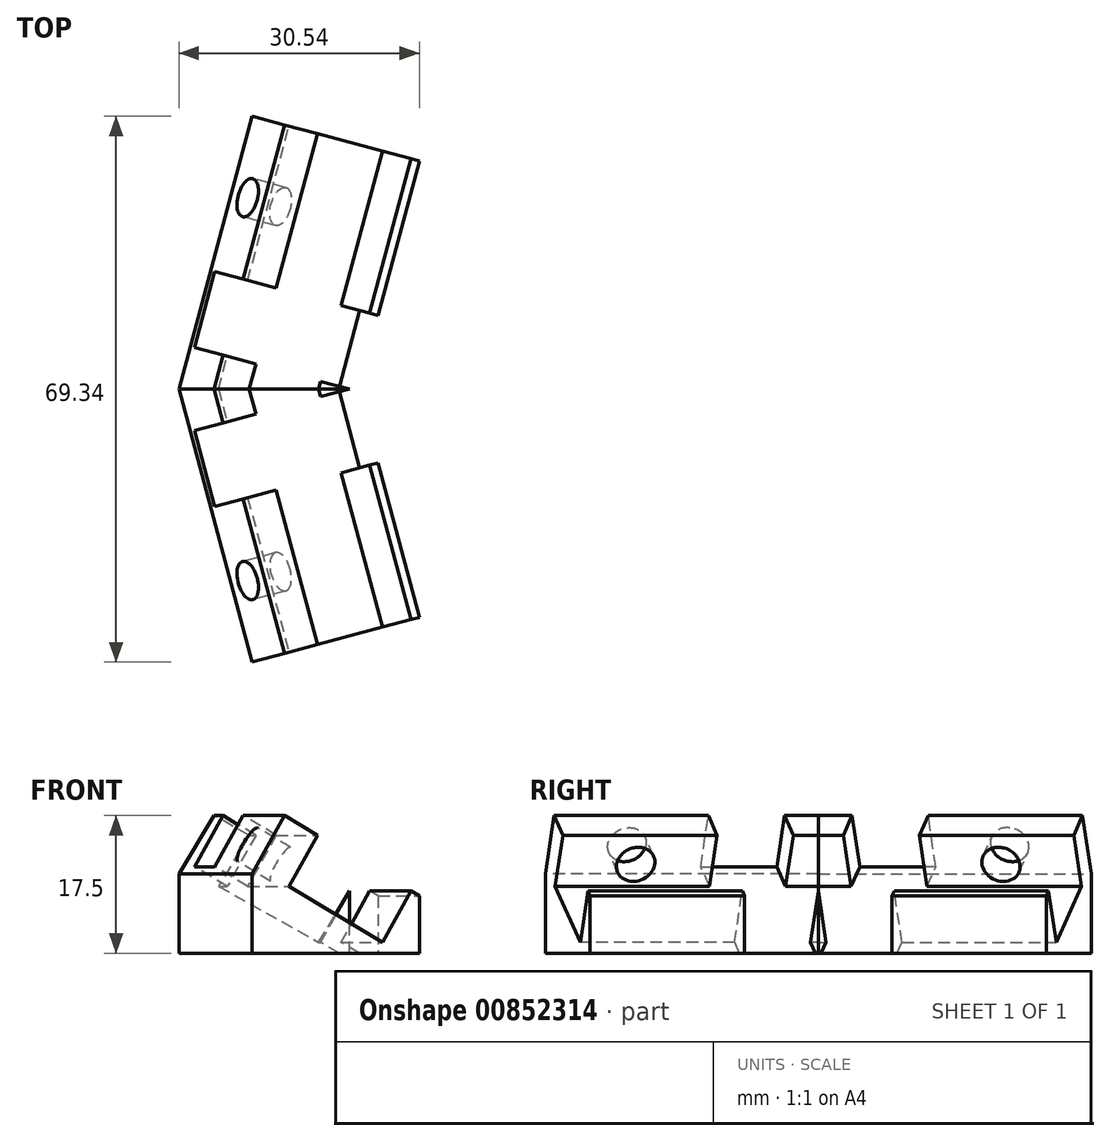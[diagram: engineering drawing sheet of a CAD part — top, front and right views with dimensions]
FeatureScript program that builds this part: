
annotation { "Feature Type Name" : "Feature", "Feature Type Description" : "" }
export const myFeature = defineFeature(function(context is Context, id is Id, definition is map)
    precondition{}
    {
        {
            var Q0;
            Q0=qCreatedBy(makeId("Top.planeOp"),FACE);
            var sketch = newSketch(context, id + "F0", { "sketchPlane" : qUnion([Q0])});
            skLineSegment(sketch, "E0", {"start": v(0, 0) * mm, "end": v(7.76, 28.98) * mm});
            skLineSegment(sketch, "E1", {"start": v(7.76, 28.98) * mm, "end": v(-13.49, 34.67) * mm});
            skLineSegment(sketch, "E2", {"start": v(-13.49, 34.67) * mm, "end": v(-22.78, 0) * mm});
            skLineSegment(sketch, "E3", {"start": v(-22.78, 0) * mm, "end": v(-13.49, -34.67) * mm});
            skLineSegment(sketch, "E4", {"start": v(-13.49, -34.67) * mm, "end": v(7.76, -28.98) * mm});
            skLineSegment(sketch, "E5", {"start": v(7.76, -28.98) * mm, "end": v(0, 0) * mm});
            skSolve(sketch);
        }
        {
            var Q0;
            Q0=makeQuery(id+"F0.imprint","IMPRINT",FACE,{"disambiguationData":[TD([[makeQuery(id+"F0.imprint","IMPRINT",EDGE,{"derivedFrom":sQuery(id+"F0.wireOp",EDGE,"E0")}),1.0]])]});
            extrude(context, id + "F1", {"entities" : qUnion([Q0]), "depth" : 20 * mm, "offsetDistance" : 25 * mm});
        }
        {
            var Q0;
            Q0=makeQuery(id+"F1.opExtrude","CAP_VERTEX",VERTEX,{"disambiguationData":[OSD([sQuery(id+"F0.wireOp",EDGE,"E0"),sQuery(id+"F0.wireOp",EDGE,"E5")])],"isStart":false});
            var Q1;
            Q1=makeQuery(id+"F1.opExtrude","CAP_VERTEX",VERTEX,{"disambiguationData":[OSD([sQuery(id+"F0.wireOp",EDGE,"E2"),sQuery(id+"F0.wireOp",EDGE,"E3")])],"isStart":false});
            var Q2;
            Q2=makeQuery(id+"F1.opExtrude","CAP_VERTEX",VERTEX,{"disambiguationData":[OSD([sQuery(id+"F0.wireOp",EDGE,"E2"),sQuery(id+"F0.wireOp",EDGE,"E3")])],"isStart":true});
            cPlane(context, id + "F2", {"entities" : qUnion([Q0, Q1, Q2]), "cplaneType" : CPlaneType.THREE_POINT, "offset" : 25 * mm, "width" : 150 * mm, "height" : 150 * mm});
        }
        {
            var Q0;
            Q0=makeQuery(id+"F1.opExtrude","SWEPT_FACE",FACE,{"disambiguationData":[OSD([sQuery(id+"F0.wireOp",EDGE,"E4")])]});
            var sketch = newSketch(context, id + "F3", { "sketchPlane" : qUnion([Q0])});
            skLineSegment(sketch, "E6", {"start": v(-17.15, 8.5) * mm, "end": v(-4.85, 1.4) * mm});
            skLineSegment(sketch, "E7", {"start": v(-4.85, 1.4) * mm, "end": v(-1.1, 7.9) * mm});
            skLineSegment(sketch, "E8", {"start": v(-1.1, 7.9) * mm, "end": v(-13.4, 15) * mm, "construction": true});
            skLineSegment(sketch, "E9", {"start": v(-13.4, 15) * mm, "end": v(-17.15, 8.5) * mm});
            skLineSegment(sketch, "E10", {"start": v(-1.1, 7.9) * mm, "end": v(0, 7.9) * mm});
            skLineSegment(sketch, "E11", {"start": v(-11, 4.95) * mm, "end": v(-11, 0) * mm, "construction": true});
            skLineSegment(sketch, "E12", {"start": v(-13.4, 15) * mm, "end": v(-13.4, 20) * mm});
            skSolve(sketch);
        }
        {
            var Q0;
            Q0=makeQuery(id+"F3.imprint","IMPRINT",FACE,{"disambiguationData":[TD([[makeQuery(id+"F3.imprint","IMPRINT",EDGE,{"derivedFrom":sQuery(id+"F3.wireOp",EDGE,"E6")}),1.0]])]});
            var Q1;
            Q1=qCreatedBy(id+"F2.planeOp",FACE);
            var Q2;
            Q2=makeQuery(id+"F1.opExtrude","CAP_VERTEX",VERTEX,{"disambiguationData":[OSD([sQuery(id+"F0.wireOp",EDGE,"E2"),sQuery(id+"F0.wireOp",EDGE,"E3")])],"isStart":false});
            extrude(context, id + "F4", {"entities" : qUnion([Q0]), "operationType" : NewBodyOperationType.REMOVE, "endBound" : BoundingType.UP_TO_SURFACE, "oppositeDirection" : true, "depth" : 35.2 * mm, "endBoundEntityFace" : qUnion([Q1]), "offsetDistance" : 25 * mm});
        }
        {
            var Q0;
            Q0=makeQuery(id+"F1.opExtrude","SWEPT_FACE",FACE,{"disambiguationData":[OSD([sQuery(id+"F0.wireOp",EDGE,"E4")])]});
            var sketch = newSketch(context, id + "F5", { "sketchPlane" : qUnion([Q0])});
            skLineSegment(sketch, "E13", {"start": v(-15.27, 11.75) * mm, "end": v(-19.6, 14.25) * mm, "construction": true});
            skLineSegment(sketch, "E14", {"start": v(-22, 10.1) * mm, "end": v(-17.73, 17.5) * mm});
            skLineSegment(sketch, "E15", {"start": v(-13.4, 15) * mm, "end": v(-17.73, 17.5) * mm});
            skSolve(sketch);
        }
        {
            var Q0;
            {var subQ2=sQuery(id+"F5.wireOp",EDGE,"E14");Q0=makeQuery(id+"F5.imprint","IMPRINT",FACE,{"disambiguationData":[TD([[makeQuery(id+"F5.imprint","IMPRINT",EDGE,{"derivedFrom":subQ2}),1.0]])]});}
            var Q1;
            Q1=qCreatedBy(id+"F2.planeOp",FACE);
            var Q2;
            Q2=makeQuery(id+"F1.opExtrude","CAP_VERTEX",VERTEX,{"disambiguationData":[OSD([sQuery(id+"F0.wireOp",EDGE,"E2"),sQuery(id+"F0.wireOp",EDGE,"E3")])],"isStart":false});
            extrude(context, id + "F6", {"entities" : qUnion([Q0]), "operationType" : NewBodyOperationType.REMOVE, "endBound" : BoundingType.UP_TO_SURFACE, "oppositeDirection" : true, "depth" : 37.1 * mm, "endBoundEntityFace" : qUnion([Q1]), "endBoundEntityVertex" : qUnion([Q2]), "offsetDistance" : 25 * mm});
        }
        {
            var Q0;
            Q0=makeQuery(id+"F4.boolean.opBoolean","COPY",FACE,{"derivedFrom":makeQuery(id+"F4.opExtrude","SWEPT_FACE",FACE,{"disambiguationData":[OSD([sQuery(id+"F3.wireOp",EDGE,"E9")])]})});
            var sketch = newSketch(context, id + "F7", { "sketchPlane" : qUnion([Q0])});
            skLineSegment(sketch, "E16", {"start": v(-36.83, 11.28) * mm, "end": v(-28.9, 10.22) * mm});
            skLineSegment(sketch, "E17", {"start": v(-28.9, 10.22) * mm, "end": v(-29.9, 2.79) * mm});
            skLineSegment(sketch, "E18", {"start": v(-29.9, 2.79) * mm, "end": v(-37.82, 3.85) * mm});
            skLineSegment(sketch, "E19", {"start": v(-37.82, 3.85) * mm, "end": v(-36.83, 11.28) * mm});
            skSolve(sketch);
        }
        {
            var Q0;
            Q0=makeQuery(id+"F7.imprint","IMPRINT",FACE,{"disambiguationData":[TD([[makeQuery(id+"F7.imprint","IMPRINT",EDGE,{"derivedFrom":sQuery(id+"F7.wireOp",EDGE,"E16")}),-1.0]])]});
            extrude(context, id + "F8", {"entities" : qUnion([Q0]), "operationType" : NewBodyOperationType.REMOVE, "endBound" : BoundingType.THROUGH_ALL, "oppositeDirection" : true, "depth" : 25 * mm, "offsetDistance" : 25 * mm, "hasSecondDirection" : true, "secondDirectionOppositeDirection" : false, "secondDirectionDepth" : 25 * mm});
        }
        {
            var Q0;
            Q0=makeQuery(id+"F1.opExtrude","SWEPT_FACE",FACE,{"disambiguationData":[OSD([sQuery(id+"F0.wireOp",EDGE,"E4")])]});
            var sketch = newSketch(context, id + "F9", { "sketchPlane" : qUnion([Q0])});
            skLineSegment(sketch, "E20", {"start": v(-1.1, 7.9) * mm, "end": v(0, 7.26) * mm});
            skSolve(sketch);
        }
        {
            var Q0;
            {var subQ0=sQuery(id+"F9.wireOp",EDGE,"E20");Q0=makeQuery(id+"F9.imprint","IMPRINT",FACE,{"disambiguationData":[TD([[makeQuery(id+"F9.imprint","IMPRINT",EDGE,{"derivedFrom":subQ0}),1.0]])]});}
            var Q1;
            Q1=qCreatedBy(id+"F2.planeOp",FACE);
            extrude(context, id + "F10", {"entities" : qUnion([Q0]), "operationType" : NewBodyOperationType.REMOVE, "endBound" : BoundingType.UP_TO_SURFACE, "oppositeDirection" : true, "depth" : 25 * mm, "endBoundEntityFace" : qUnion([Q1]), "offsetDistance" : 25 * mm});
        }
        {
            var Q0;
            Q0=makeQuery(id+"F4.boolean.opBoolean","COPY",FACE,{"derivedFrom":makeQuery(id+"F4.opExtrude","SWEPT_FACE",FACE,{"disambiguationData":[OSD([sQuery(id+"F3.wireOp",EDGE,"E7")])]})});
            var sketch = newSketch(context, id + "F11", { "sketchPlane" : qUnion([Q0])});
            skLineSegment(sketch, "E21", {"start": v(-1.13, 6.2) * mm, "end": v(-0.13, -1.24) * mm});
            skLineSegment(sketch, "E22", {"start": v(-1.13, 6.2) * mm, "end": v(8.78, 7.52) * mm});
            skLineSegment(sketch, "E23", {"start": v(8.78, 7.52) * mm, "end": v(9.78, 0.1) * mm});
            skLineSegment(sketch, "E24", {"start": v(9.78, 0.1) * mm, "end": v(-0.13, -1.24) * mm});
            skSolve(sketch);
        }
        {
            var Q0;
            Q0=makeQuery(id+"F11.imprint","IMPRINT",FACE,{"disambiguationData":[TD([[makeQuery(id+"F11.imprint","IMPRINT",EDGE,{"derivedFrom":sQuery(id+"F11.wireOp",EDGE,"E21")}),1.0]])]});
            extrude(context, id + "F12", {"entities" : qUnion([Q0]), "operationType" : NewBodyOperationType.REMOVE, "endBound" : BoundingType.THROUGH_ALL, "oppositeDirection" : true, "depth" : 25 * mm, "offsetDistance" : 25 * mm, "hasSecondDirection" : true, "secondDirectionBound" : SecondDirectionBoundingType.THROUGH_ALL, "secondDirectionOppositeDirection" : false, "secondDirectionDepth" : 25 * mm});
        }
        {
            var Q0;
            Q0=makeQuery(id+"F6.boolean.opBoolean","COPY",FACE,{"derivedFrom":makeQuery(id+"F6.opExtrude","SWEPT_FACE",FACE,{"disambiguationData":[OSD([sQuery(id+"F5.wireOp",EDGE,"E14")])]})});
            var sketch = newSketch(context, id + "F13", { "sketchPlane" : qUnion([Q0])});
            skCircle(sketch, "E25", {"center": v(19.4, 4.64) * mm, "radius": 2.5 * mm});
            skLineSegment(sketch, "E26", {"start": v(19.4, 4.64) * mm, "end": v(29.47, 5.99) * mm, "construction": true});
            skLineSegment(sketch, "E27", {"start": v(19.4, 4.64) * mm, "end": v(18.84, 8.87) * mm, "construction": true});
            skSolve(sketch);
        }
        {
            var Q0;
            Q0=makeQuery(id+"F13.imprint","IMPRINT",FACE,{"disambiguationData":[TD([[makeQuery(id+"F13.imprint","IMPRINT",EDGE,{"derivedFrom":sQuery(id+"F13.wireOp",EDGE,"E25")}),1.0]])]});
            extrude(context, id + "F14", {"entities" : qUnion([Q0]), "operationType" : NewBodyOperationType.REMOVE, "endBound" : BoundingType.UP_TO_NEXT, "oppositeDirection" : true, "depth" : 25 * mm, "offsetDistance" : 25 * mm});
        }
        {
            var Q0;
            Q0=makeQuery(id+"F1.opExtrude","SWEPT_BODY",BODY,{"disambiguationData":[OSD([sQuery(id+"F0.wireOp",EDGE,"E0"),sQuery(id+"F0.wireOp",EDGE,"E1"),sQuery(id+"F0.wireOp",EDGE,"E2"),sQuery(id+"F0.wireOp",EDGE,"E3"),sQuery(id+"F0.wireOp",EDGE,"E4"),sQuery(id+"F0.wireOp",EDGE,"E5")])]});
            var Q1;
            Q1=qCreatedBy(makeId("Front.planeOp"),FACE);
            mirror(context, id + "F15", {"operationType" : NewBodyOperationType.INTERSECT, "entities" : qUnion([Q0]), "mirrorPlane" : qUnion([Q1])});
        }
    });
